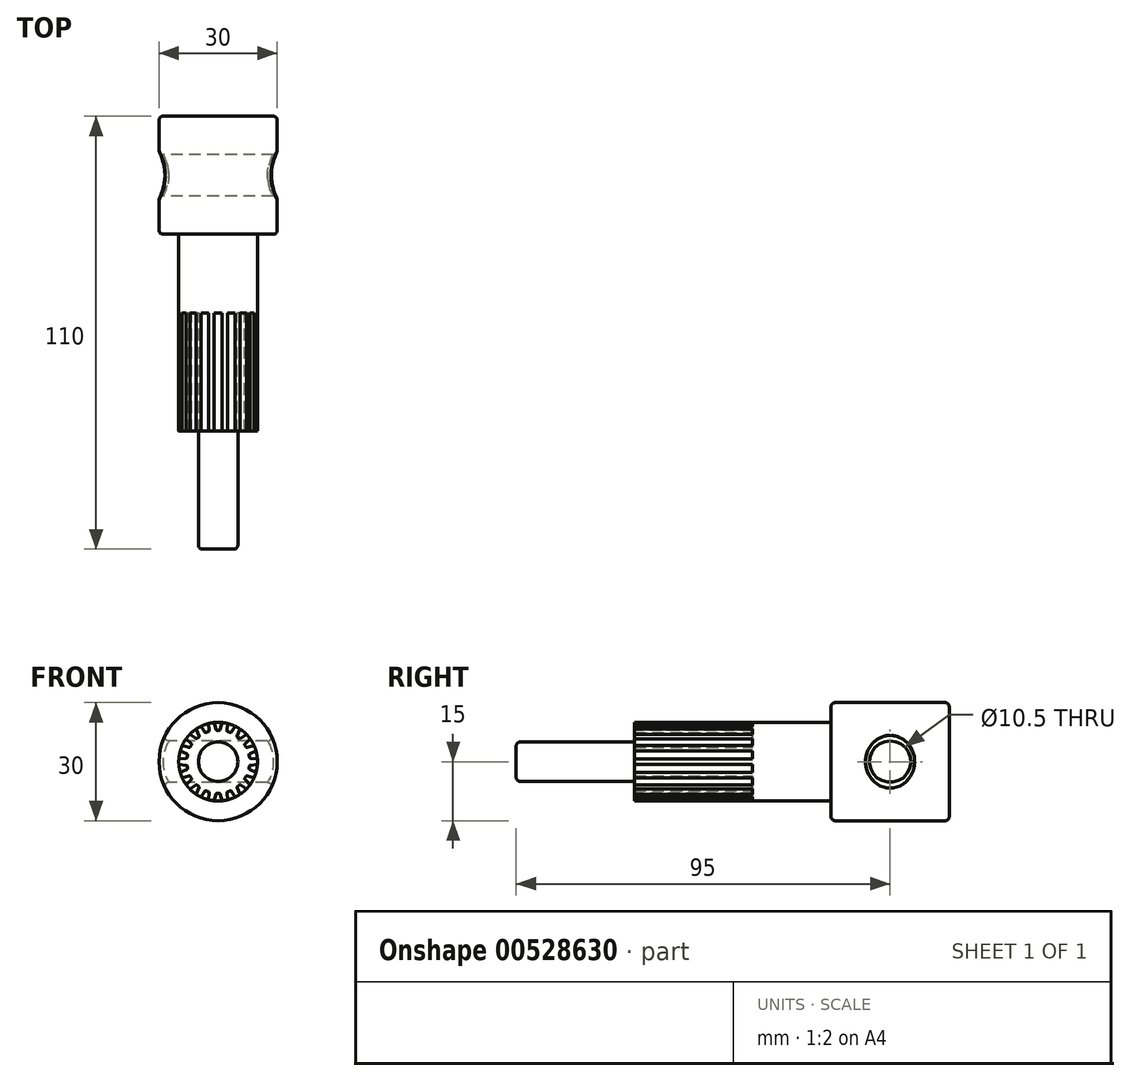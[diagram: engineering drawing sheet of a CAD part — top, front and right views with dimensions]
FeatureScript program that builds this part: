
annotation { "Feature Type Name" : "Feature", "Feature Type Description" : "" }
export const myFeature = defineFeature(function(context is Context, id is Id, definition is map)
    precondition{}
    {
        {
            var Q0;
            Q0=qCreatedBy(makeId("Front.planeOp"),FACE);
            var sketch = newSketch(context, id + "F0", { "sketchPlane" : qUnion([Q0])});
            skCircle(sketch, "E0", {"center": v(0, 0) * mm, "radius": 10 * mm});
            skSolve(sketch);
        }
        {
            var Q0;
            Q0=makeQuery(id+"F0.imprint","IMPRINT",FACE,{"disambiguationData":[TD([[makeQuery(id+"F0.imprint","IMPRINT",EDGE,{"derivedFrom":sQuery(id+"F0.wireOp",EDGE,"E0")}),1.0]])]});
            extrude(context, id + "F1", {"entities" : qUnion([Q0]), "depth" : 30 * mm, "offsetDistance" : 25 * mm});
        }
        {
            var Q0;
            Q0=makeQuery(id+"F1.opExtrude","CAP_FACE",FACE,{"disambiguationData":[OSD([sQuery(id+"F0.wireOp",EDGE,"E0")])],"isStart":false});
            var sketch = newSketch(context, id + "F2", { "sketchPlane" : qUnion([Q0])});
            skCircle(sketch, "E1.0.0", {"center": v(0, 0) * mm, "radius": 10 * mm});
            skArc(sketch, "E2", {"start": v(1, 9.95) * mm, "mid": v(0, 10.05) * mm, "end": v(-1, 9.95) * mm});
            skLineSegment(sketch, "E3", {"start": v(-0.5, 8) * mm, "end": v(0.5, 8) * mm});
            skLineSegment(sketch, "E4", {"start": v(0.5, 8) * mm, "end": v(1, 9.95) * mm});
            skLineSegment(sketch, "E5", {"start": v(-1, 9.95) * mm, "end": v(-0.5, 8) * mm});
            skSolve(sketch);
        }
        {
            var Q0;
            Q0=makeQuery(id+"F2.imprint","IMPRINT",FACE,{"disambiguationData":[TD([[makeQuery(id+"F2.imprint","IMPRINT",EDGE,{"derivedFrom":sQuery(id+"F2.wireOp",EDGE,"E3")}),1.0]])]});
            var Q1;
            {var subQ0=sQuery(id+"F2.wireOp",EDGE,"E2");Q1=makeQuery(id+"F2.imprint","IMPRINT",FACE,{"disambiguationData":[TD([[makeQuery(id+"F2.imprint","IMPRINT",EDGE,{"derivedFrom":subQ0}),1.0]])]});}
            extrude(context, id + "F3", {"entities" : qUnion([Q0, Q1]), "operationType" : NewBodyOperationType.REMOVE, "oppositeDirection" : true, "depth" : 50 * mm, "offsetDistance" : 25 * mm});
        }
        {
            var Q0;
            Q0=makeQuery(id+"F3.boolean.opBoolean","COPY",EDGE,{"derivedFrom":makeQuery(id+"F3.opExtrude","SWEPT_EDGE",EDGE,{"disambiguationData":[OSD([sQuery(id+"F2.wireOp",EDGE,"E3"),sQuery(id+"F2.wireOp",EDGE,"E5")])]})});
            var Q1;
            Q1=makeQuery(id+"F3.boolean.opBoolean","COPY",EDGE,{"derivedFrom":makeQuery(id+"F3.opExtrude","SWEPT_EDGE",EDGE,{"disambiguationData":[OSD([sQuery(id+"F2.wireOp",EDGE,"E3"),sQuery(id+"F2.wireOp",EDGE,"E4")])]})});
            var Q2;
            Q2=makeQuery(id+"F3.boolean.opBoolean","COPY",EDGE,{"derivedFrom":makeQuery(id+"F3.opExtrude","SWEPT_EDGE",EDGE,{"disambiguationData":[OSD([sQuery(id+"F2.wireOp",EDGE,"E1.0.0"),sQuery(id+"F2.wireOp",EDGE,"E2"),sQuery(id+"F2.wireOp",EDGE,"E5")])]})});
            var Q3;
            Q3=makeQuery(id+"F3.boolean.opBoolean","COPY",EDGE,{"derivedFrom":makeQuery(id+"F3.opExtrude","SWEPT_EDGE",EDGE,{"disambiguationData":[OSD([sQuery(id+"F2.wireOp",EDGE,"E1.0.0"),sQuery(id+"F2.wireOp",EDGE,"E2"),sQuery(id+"F2.wireOp",EDGE,"E4")])]})});
            fillet(context, id + "F4", {"entities" : qUnion([Q0, Q1, Q2, Q3]), "radius" : .2 * mm, "tangentPropagation" : true, "allowEdgeOverflow" : false});
        }
        {
            var Q0;
            Q0=makeQuery(id+"F3.opExtrude","SWEPT_BODY",BODY,{"disambiguationData":[OSD([sQuery(id+"F2.wireOp",EDGE,"E2"),sQuery(id+"F2.wireOp",EDGE,"E3"),sQuery(id+"F2.wireOp",EDGE,"E4"),sQuery(id+"F2.wireOp",EDGE,"E5")])]});
            var Q1;
            Q1=makeQuery(id+"F4.opFillet","BLEND_FACE",FACE,{"disambiguationData":[OSD([sQuery(id+"F2.wireOp",EDGE,"E1.0.0"),sQuery(id+"F2.wireOp",EDGE,"E2"),sQuery(id+"F2.wireOp",EDGE,"E5")])]});
            var Q2;
            Q2=makeQuery(id+"F3.boolean.opBoolean","COPY",FACE,{"derivedFrom":makeQuery(id+"F3.opExtrude","SWEPT_FACE",FACE,{"disambiguationData":[OSD([sQuery(id+"F2.wireOp",EDGE,"E5")])]})});
            var Q3;
            Q3=makeQuery(id+"F4.opFillet","BLEND_FACE",FACE,{"disambiguationData":[OSD([sQuery(id+"F2.wireOp",EDGE,"E3"),sQuery(id+"F2.wireOp",EDGE,"E5")])]});
            var Q4;
            Q4=makeQuery(id+"F3.boolean.opBoolean","COPY",FACE,{"derivedFrom":makeQuery(id+"F3.opExtrude","SWEPT_FACE",FACE,{"disambiguationData":[OSD([sQuery(id+"F2.wireOp",EDGE,"E3")])]})});
            var Q5;
            Q5=makeQuery(id+"F4.opFillet","BLEND_FACE",FACE,{"disambiguationData":[OSD([sQuery(id+"F2.wireOp",EDGE,"E3"),sQuery(id+"F2.wireOp",EDGE,"E4")])]});
            var Q6;
            Q6=makeQuery(id+"F3.boolean.opBoolean","COPY",FACE,{"derivedFrom":makeQuery(id+"F3.opExtrude","SWEPT_FACE",FACE,{"disambiguationData":[OSD([sQuery(id+"F2.wireOp",EDGE,"E4")])]})});
            var Q7;
            Q7=makeQuery(id+"F4.opFillet","BLEND_FACE",FACE,{"disambiguationData":[OSD([sQuery(id+"F2.wireOp",EDGE,"E1.0.0"),sQuery(id+"F2.wireOp",EDGE,"E2"),sQuery(id+"F2.wireOp",EDGE,"E4")])]});
            var Q8;
            Q8=makeQuery(id+"F1.opExtrude","SWEPT_FACE",FACE,{"disambiguationData":[OSD([sQuery(id+"F0.wireOp",EDGE,"E0")])]});
            circularPattern(context, id + "F5", {"patternType" : PatternType.FACE, "operationType" : NewBodyOperationType.REMOVE, "faces" : qUnion([Q1, Q2, Q3, Q4, Q5, Q6, Q7]), "axis" : qUnion([Q8]), "angle" : 360 * degree, "instanceCount" : 18, "equalSpace" : true});
        }
        {
            var Q0;
            Q0=makeQuery(id+"F0.imprint","IMPRINT",FACE,{"disambiguationData":[TD([[makeQuery(id+"F0.imprint","IMPRINT",EDGE,{"derivedFrom":sQuery(id+"F0.wireOp",EDGE,"2KcSvOYh-WTDN-ZqFQ-1rCm-kn9CLWwSmm2u")}),1.0]])]});
            var Q1;
            Q1=makeQuery(id+"F0.imprint","IMPRINT",FACE,{"disambiguationData":[TD([[makeQuery(id+"F0.imprint","IMPRINT",EDGE,{"derivedFrom":sQuery(id+"F0.wireOp",EDGE,"E0")}),1.0]])]});
            extrude(context, id + "F6", {"entities" : qUnion([Q0, Q1]), "operationType" : NewBodyOperationType.ADD, "oppositeDirection" : true, "depth" : 20 * mm, "offsetDistance" : 25 * mm});
        }
        {
            var Q0;
            Q0=makeQuery(id+"F1.opExtrude","CAP_FACE",FACE,{"disambiguationData":[OSD([sQuery(id+"F0.wireOp",EDGE,"E0")])],"isStart":false});
            var sketch = newSketch(context, id + "F7", { "sketchPlane" : qUnion([Q0])});
            skCircle(sketch, "E6", {"center": v(0, 0) * mm, "radius": 5 * mm});
            skSolve(sketch);
        }
        {
            var Q0;
            Q0=makeQuery(id+"F7.imprint","IMPRINT",FACE,{"disambiguationData":[TD([[makeQuery(id+"F7.imprint","IMPRINT",EDGE,{"derivedFrom":sQuery(id+"F7.wireOp",EDGE,"E6")}),1.0]])]});
            extrude(context, id + "F8", {"entities" : qUnion([Q0]), "operationType" : NewBodyOperationType.ADD, "depth" : 30 * mm, "offsetDistance" : 25 * mm});
        }
        {
            var Q0;
            Q0=makeQuery(id+"F6.opExtrude","CAP_FACE",FACE,{"disambiguationData":[OSD([sQuery(id+"F0.wireOp",EDGE,"E0")])],"isStart":false});
            var sketch = newSketch(context, id + "F9", { "sketchPlane" : qUnion([Q0])});
            skCircle(sketch, "E7", {"center": v(0, 0) * mm, "radius": 15 * mm});
            skSolve(sketch);
        }
        {
            var Q0;
            Q0=makeQuery(id+"F9.imprint","IMPRINT",FACE,{"disambiguationData":[TD([[makeQuery(id+"F9.imprint","IMPRINT",EDGE,{"derivedFrom":sQuery(id+"F9.wireOp",EDGE,"E7")}),1.0]])]});
            var Q1;
            Q1=makeQuery(id+"F9.imprint","IMPRINT",FACE,{"disambiguationData":[TD([[makeQuery(id+"F9.imprint","IMPRINT",EDGE,{"derivedFrom":makeQuery(id+"F6.opExtrude","CAP_EDGE",EDGE,{"disambiguationData":[OSD([sQuery(id+"F0.wireOp",EDGE,"E0")])],"isStart":false})}),-1.0]])]});
            extrude(context, id + "F10", {"entities" : qUnion([Q0, Q1]), "operationType" : NewBodyOperationType.ADD, "depth" : 30 * mm, "offsetDistance" : 25 * mm});
        }
        {
            var Q0;
            Q0=qCreatedBy(makeId("Right.planeOp"),FACE);
            var sketch = newSketch(context, id + "F11", { "sketchPlane" : qUnion([Q0])});
            skCircle(sketch, "E8", {"center": v(35, 0) * mm, "radius": 5.25 * mm});
            skSolve(sketch);
        }
        {
            var Q0;
            Q0 = qSketchRegion(id + "F11", true);
            extrude(context, id + "F12", {"entities" : qUnion([Q0]), "operationType" : NewBodyOperationType.REMOVE, "endBound" : BoundingType.SYMMETRIC, "depth" : 50 * mm, "offsetDistance" : 25 * mm});
        }
        {
            var Q0;
            Q0=makeQuery(id+"F10.opExtrude","CAP_EDGE",EDGE,{"disambiguationData":[OSD([sQuery(id+"F9.wireOp",EDGE,"E7")])],"isStart":true});
            var Q1;
            Q1=makeQuery(id+"F12.boolean.opBoolean","COPY",FACE,{"derivedFrom":makeQuery(id+"F12.opExtrude","SWEPT_FACE",FACE,{"disambiguationData":[OSD([sQuery(id+"F11.wireOp",EDGE,"E8")])]})});
            var Q2;
            Q2=makeQuery(id+"F10.opExtrude","CAP_EDGE",EDGE,{"disambiguationData":[OSD([sQuery(id+"F9.wireOp",EDGE,"E7")])],"isStart":false});
            var Q3;
            Q3=makeQuery(id+"F8.opExtrude","CAP_EDGE",EDGE,{"disambiguationData":[OSD([sQuery(id+"F7.wireOp",EDGE,"E6")])],"isStart":false});
            fillet(context, id + "F13", {"entities" : qUnion([Q0, Q1, Q2, Q3]), "radius" : 1 * mm, "tangentPropagation" : true, "allowEdgeOverflow" : false});
        }
    });
